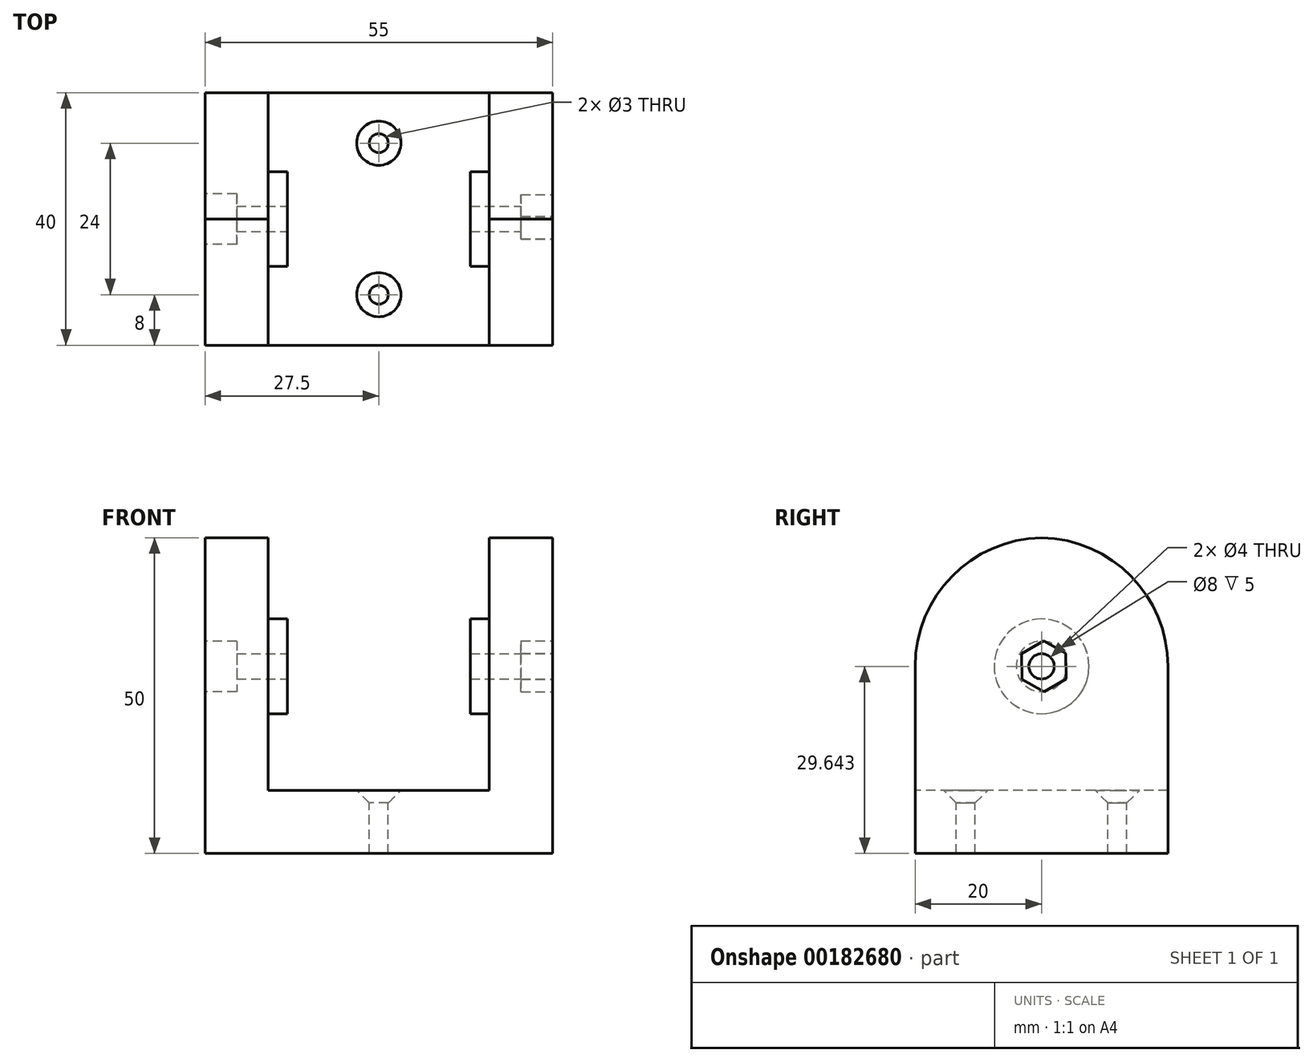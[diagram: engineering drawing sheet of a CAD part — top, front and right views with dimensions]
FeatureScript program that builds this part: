
annotation { "Feature Type Name" : "Feature", "Feature Type Description" : "" }
export const myFeature = defineFeature(function(context is Context, id is Id, definition is map)
    precondition{}
    {
        {
            var Q0;
            Q0=qCreatedBy(makeId("Top.planeOp"),FACE);
            var sketch = newSketch(context, id + "F0", { "sketchPlane" : qUnion([Q0])});
            skLineSegment(sketch, "E0.rect.bottom", {"start": v(27.5, -20) * mm, "end": v(-27.5, -20) * mm});
            skLineSegment(sketch, "E0.rect.top", {"start": v(27.5, 20) * mm, "end": v(-27.5, 20) * mm});
            skLineSegment(sketch, "E0.rect.left", {"start": v(27.5, -20) * mm, "end": v(27.5, 20) * mm});
            skLineSegment(sketch, "E0.rect.right", {"start": v(-27.5, -20) * mm, "end": v(-27.5, 20) * mm});
            skPoint(sketch, "E0.rect.middle", {"position": v(0, 0) * mm});
            skSolve(sketch);
        }
        {
            var Q0;
            Q0=qSketchRegion(id+"F0",true);
            extrude(context, id + "F12", {"entities" : qUnion([Q0]), "depth" : 50 * mm});
        }
        {
            var Q0;
            Q0=makeQuery(id+"F12.opExtrude","SWEPT_FACE",FACE,{"disambiguationData":[OSD([sQuery(id+"F0.wireOp",EDGE,"E0.rect.bottom")])]});
            var sketch = newSketch(context, id + "F1", { "sketchPlane" : qUnion([Q0])});
            skLineSegment(sketch, "E1.bottom", {"start": v(-17.5, 50) * mm, "end": v(17.5, 50) * mm});
            skLineSegment(sketch, "E1.top", {"start": v(-17.5, 10) * mm, "end": v(17.5, 10) * mm});
            skLineSegment(sketch, "E1.left", {"start": v(-17.5, 50) * mm, "end": v(-17.5, 10) * mm});
            skLineSegment(sketch, "E1.right", {"start": v(17.5, 50) * mm, "end": v(17.5, 10) * mm});
            skSolve(sketch);
        }
        {
            var Q0;
            Q0=qSketchRegion(id+"F1",true);
            extrude(context, id + "F13", {"entities" : qUnion([Q0]), "operationType" : NewBodyOperationType.REMOVE, "endBound" : BoundingType.THROUGH_ALL, "oppositeDirection" : true, "depth" : 25 * mm});
        }
        {
            var Q0;
            {var subQ0=sQuery(id+"F0.wireOp",EDGE,"E0.rect.bottom");var subQ1=sQuery(id+"F0.wireOp",EDGE,"E0.rect.left");Q0=makeQuery(id+"F13.boolean.opBoolean","SPLIT",EDGE,{"disambiguationData":[TD([makeQuery(id+"F12.opExtrude","SWEPT_FACE",FACE,{"disambiguationData":[OSD([subQ1])]})])],"derivedFrom":makeQuery(id+"F12.opExtrude","CAP_EDGE",EDGE,{"disambiguationData":[OSD([subQ0])],"isStart":false})});}
            var Q1;
            {var subQ0=sQuery(id+"F0.wireOp",EDGE,"E0.rect.bottom");var subQ1=sQuery(id+"F0.wireOp",EDGE,"E0.rect.right");Q1=makeQuery(id+"F13.boolean.opBoolean","SPLIT",EDGE,{"disambiguationData":[TD([makeQuery(id+"F12.opExtrude","SWEPT_FACE",FACE,{"disambiguationData":[OSD([subQ1])]})])],"derivedFrom":makeQuery(id+"F12.opExtrude","CAP_EDGE",EDGE,{"disambiguationData":[OSD([subQ0])],"isStart":false})});}
            var Q2;
            {var subQ0=sQuery(id+"F0.wireOp",EDGE,"E0.rect.top");var subQ1=sQuery(id+"F0.wireOp",EDGE,"E0.rect.left");Q2=makeQuery(id+"F13.boolean.opBoolean","SPLIT",EDGE,{"disambiguationData":[TD([makeQuery(id+"F12.opExtrude","SWEPT_FACE",FACE,{"disambiguationData":[OSD([subQ1])]})])],"derivedFrom":makeQuery(id+"F12.opExtrude","CAP_EDGE",EDGE,{"disambiguationData":[OSD([subQ0])],"isStart":false})});}
            var Q3;
            {var subQ0=sQuery(id+"F0.wireOp",EDGE,"E0.rect.top");var subQ1=sQuery(id+"F0.wireOp",EDGE,"E0.rect.right");Q3=makeQuery(id+"F13.boolean.opBoolean","SPLIT",EDGE,{"disambiguationData":[TD([makeQuery(id+"F12.opExtrude","SWEPT_FACE",FACE,{"disambiguationData":[OSD([subQ1])]})])],"derivedFrom":makeQuery(id+"F12.opExtrude","CAP_EDGE",EDGE,{"disambiguationData":[OSD([subQ0])],"isStart":false})});}
            fillet(context, id + "F14", {"entities" : qUnion([Q0, Q1, Q2, Q3]), "radius" : 20.36 * mm, "tangentPropagation" : true, "allowEdgeOverflow" : false});
        }
        {
            var Q0;
            Q0=makeQuery(id+"F12.opExtrude","SWEPT_FACE",FACE,{"disambiguationData":[OSD([sQuery(id+"F0.wireOp",EDGE,"E0.rect.left")])]});
            var sketch = newSketch(context, id + "F15", { "sketchPlane" : qUnion([Q0])});
            skCircle(sketch, "E2", {"center": v(0, 29.64) * mm, "radius": 2 * mm});
            skSolve(sketch);
        }
        {
            var Q0;
            Q0=qSketchRegion(id+"F15",true);
            extrude(context, id + "F2", {"entities" : qUnion([Q0]), "operationType" : NewBodyOperationType.REMOVE, "endBound" : BoundingType.THROUGH_ALL, "oppositeDirection" : true, "depth" : 25 * mm});
        }
        {
            var Q0;
            Q0=makeQuery(id+"F13.boolean.opBoolean","COPY",FACE,{"derivedFrom":makeQuery(id+"F13.opExtrude","SWEPT_FACE",FACE,{"disambiguationData":[OSD([sQuery(id+"F1.wireOp",EDGE,"E1.left")])]})});
            var sketch = newSketch(context, id + "F3", { "sketchPlane" : qUnion([Q0])});
            skCircle(sketch, "E3", {"center": v(0, 29.64) * mm, "radius": 7.5 * mm});
            skCircle(sketch, "E4.0", {"center": v(0, 29.64) * mm, "radius": 2 * mm});
            skSolve(sketch);
        }
        {
            var Q0;
            Q0=makeQuery(id+"F3.imprint","IMPRINT",FACE,{"disambiguationData":[TD([[makeQuery(id+"F3.imprint","IMPRINT",EDGE,{"derivedFrom":sQuery(id+"F3.wireOp",EDGE,"E3")}),1.0]])]});
            extrude(context, id + "F16", {"entities" : qUnion([Q0]), "operationType" : NewBodyOperationType.ADD, "depth" : 3 * mm});
        }
        {
            var Q0;
            Q0=makeQuery(id+"F12.opExtrude","SWEPT_BODY",BODY,{"disambiguationData":[OSD([sQuery(id+"F0.wireOp",EDGE,"E0.rect.bottom"),sQuery(id+"F0.wireOp",EDGE,"E0.rect.top"),sQuery(id+"F0.wireOp",EDGE,"E0.rect.left"),sQuery(id+"F0.wireOp",EDGE,"E0.rect.right")])]});
            var Q1;
            Q1=qCreatedBy(makeId("Right.planeOp"),FACE);
            mirror(context, id + "F4", {"operationType" : NewBodyOperationType.ADD, "entities" : qUnion([Q0]), "mirrorPlane" : qUnion([Q1])});
        }
        {
            var Q0;
            Q0=makeQuery(id+"F13.boolean.opBoolean","COPY",FACE,{"derivedFrom":makeQuery(id+"F13.opExtrude","SWEPT_FACE",FACE,{"disambiguationData":[OSD([sQuery(id+"F1.wireOp",EDGE,"E1.top")])]})});
            var sketch = newSketch(context, id + "F5", { "sketchPlane" : qUnion([Q0])});
            skPoint(sketch, "E5", {"position": v(0, 12) * mm});
            skPoint(sketch, "E6", {"position": v(0, -12) * mm});
            skSolve(sketch);
        }
        {
            var Q0;
            Q0=sQuery(id+"F5.wireOp",VERTEX,"E5");
            var Q1;
            Q1=sQuery(id+"F5.wireOp",VERTEX,"E6");
            var Q2;
            Q2=makeQuery(id+"F12.opExtrude","SWEPT_BODY",BODY,{"disambiguationData":[OSD([sQuery(id+"F0.wireOp",EDGE,"E0.rect.bottom"),sQuery(id+"F0.wireOp",EDGE,"E0.rect.top"),sQuery(id+"F0.wireOp",EDGE,"E0.rect.left"),sQuery(id+"F0.wireOp",EDGE,"E0.rect.right")])]});
            hole(context, id + "F6", {"style" : HoleStyle.C_SINK, "holeDiameter" : 3 * mm, "cSinkDiameter" : 7 * mm, "endStyle" : HoleEndStyle.THROUGH, "locations" : qUnion([Q0, Q1]), "scope" : qUnion([Q2]), "cSinkAngle" : 90 * degree});
        }
        {
            var Q0;
            Q0=makeQuery(id+"F12.opExtrude","SWEPT_FACE",FACE,{"disambiguationData":[OSD([sQuery(id+"F0.wireOp",EDGE,"E0.rect.left")])]});
            var sketch = newSketch(context, id + "F7", { "sketchPlane" : qUnion([Q0])});
            skCircle(sketch, "E7.cCircle", {"center": v(0.36, 29.64) * mm, "radius": 3.5 * mm, "construction": true});
            skLineSegment(sketch, "E7.0", {"start": v(3.88, 27.66) * mm, "end": v(0.4, 25.6) * mm});
            skLineSegment(sketch, "E7.1", {"start": v(0.4, 25.6) * mm, "end": v(-3.12, 27.58) * mm});
            skLineSegment(sketch, "E7.2", {"start": v(-3.12, 27.58) * mm, "end": v(-3.17, 31.62) * mm});
            skLineSegment(sketch, "E7.3", {"start": v(-3.17, 31.62) * mm, "end": v(0.31, 33.68) * mm});
            skLineSegment(sketch, "E7.4", {"start": v(0.31, 33.68) * mm, "end": v(3.83, 31.7) * mm});
            skLineSegment(sketch, "E7.5", {"start": v(3.83, 31.7) * mm, "end": v(3.88, 27.66) * mm});
            skPoint(sketch, "E7.0.midPoint", {"position": v(2.14, 26.63) * mm});
            skSolve(sketch);
        }
        {
            var Q0;
            Q0=makeQuery(id+"F7.imprint","IMPRINT",FACE,{"disambiguationData":[TD([[makeQuery(id+"F7.imprint","IMPRINT",EDGE,{"derivedFrom":sQuery(id+"F7.wireOp",EDGE,"E7.0")}),-1.0]])]});
            extrude(context, id + "F8", {"entities" : qUnion([Q0]), "operationType" : NewBodyOperationType.REMOVE, "oppositeDirection" : true, "depth" : 5 * mm});
        }
        {
            var Q0;
            Q0=makeQuery(id+"F12.opExtrude","SWEPT_FACE",FACE,{"disambiguationData":[OSD([sQuery(id+"F0.wireOp",EDGE,"E0.rect.right")])]});
            var sketch = newSketch(context, id + "F17", { "sketchPlane" : qUnion([Q0])});
            skCircle(sketch, "E8", {"center": v(0, 29.64) * mm, "radius": 4 * mm});
            skSolve(sketch);
        }
        {
            var Q0;
            Q0=makeQuery(id+"F17.imprint","IMPRINT",FACE,{"disambiguationData":[TD([[makeQuery(id+"F17.imprint","IMPRINT",EDGE,{"derivedFrom":sQuery(id+"F17.wireOp",EDGE,"E8")}),1.0]])]});
            extrude(context, id + "F9", {"entities" : qUnion([Q0]), "operationType" : NewBodyOperationType.REMOVE, "oppositeDirection" : true, "depth" : 5 * mm});
        }
    });
